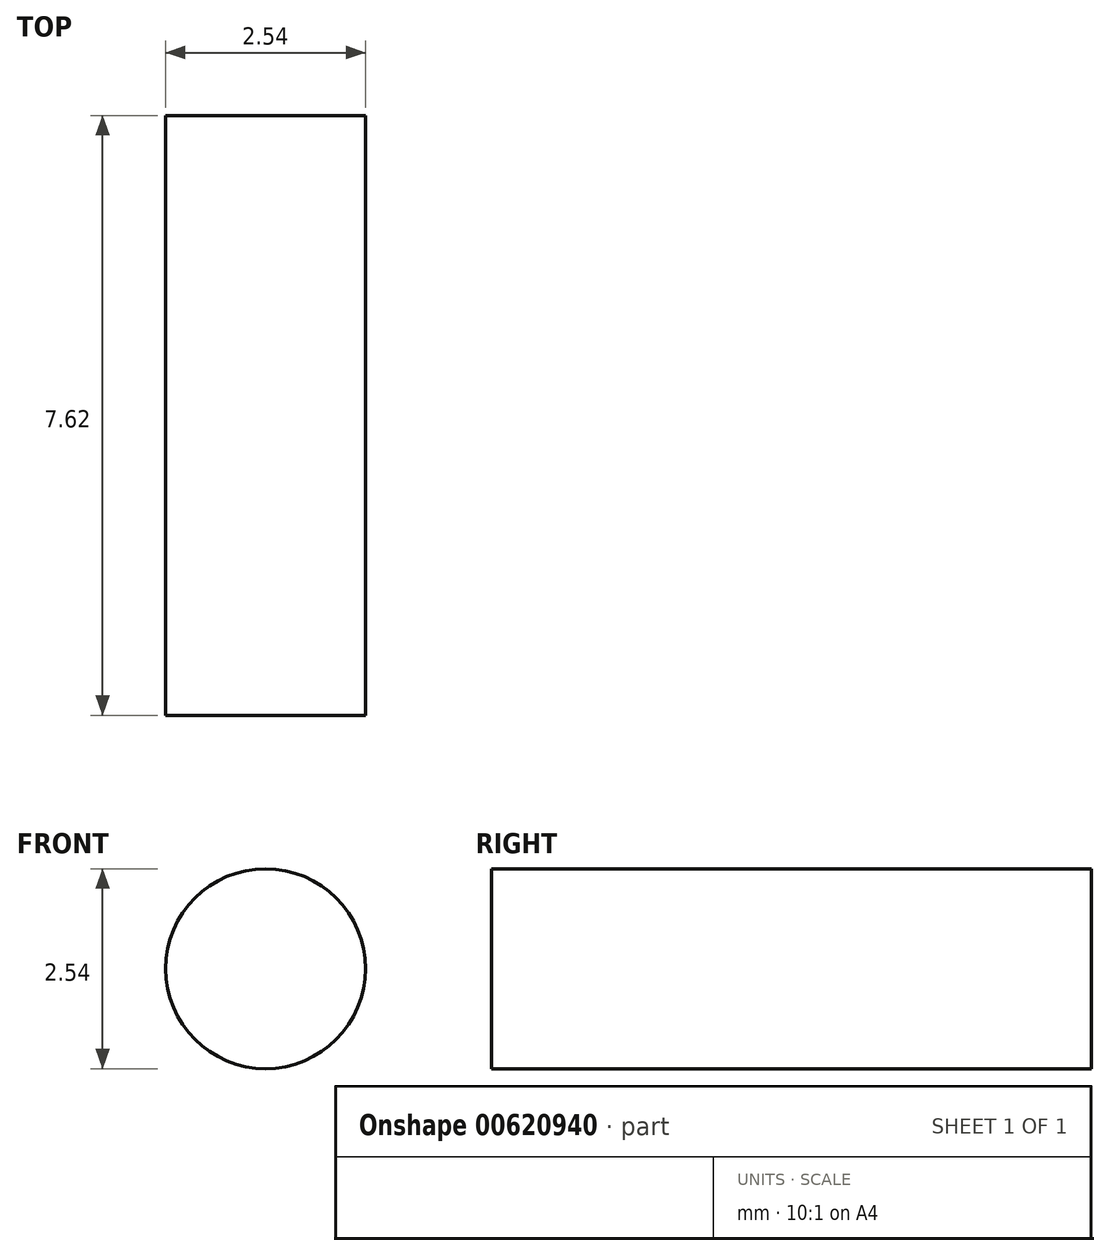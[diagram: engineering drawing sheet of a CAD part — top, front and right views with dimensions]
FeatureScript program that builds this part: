
annotation { "Feature Type Name" : "Feature", "Feature Type Description" : "" }
export const myFeature = defineFeature(function(context is Context, id is Id, definition is map)
    precondition{}
    {
        {
            var Q0;
            Q0=qCreatedBy(makeId("Front.planeOp"),FACE);
            var sketch = newSketch(context, id + "F0", { "sketchPlane" : qUnion([Q0])});
            skCircle(sketch, "E0", {"center": v(0, 0) * mm, "radius": 1.27 * mm});
            skSolve(sketch);
        }
        {
            var Q0;
            Q0=qSketchRegion(id+"F0",true);
            extrude(context, id + "F1", {"entities" : qUnion([Q0]), "depth" : 7.62 * mm, "offsetDistance" : 25.4 * mm});
        }
    });
